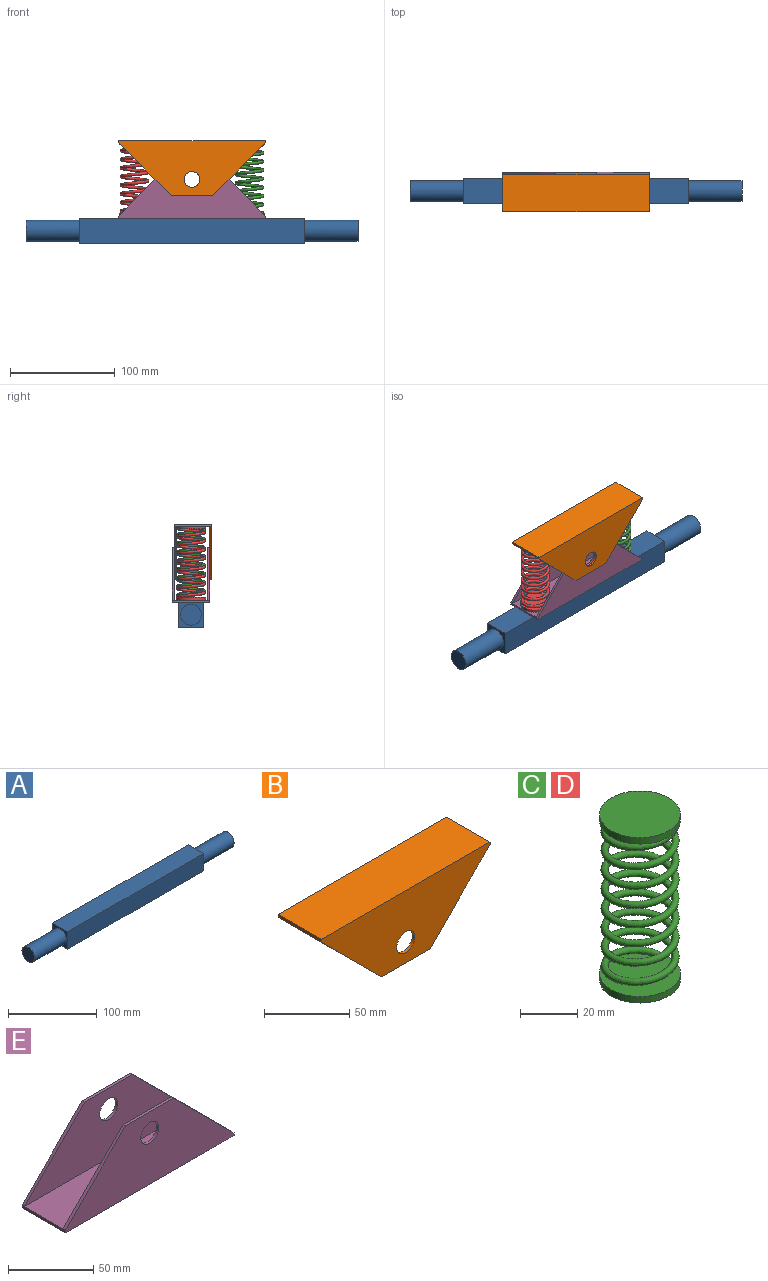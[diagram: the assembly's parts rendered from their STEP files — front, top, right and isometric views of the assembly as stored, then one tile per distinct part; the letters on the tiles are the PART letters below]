
ASSEMBLY  parts=5 mates=4
PART A: 10 faces, bbox 317.5x24x24 mm
  f0: plane 24x24mm, normal (1,0,0), area 261.8mm2, adj f2,f6,f7,f8,f9
  f1: plane 24x24mm, normal (-1,0,0), area 261.8mm2, adj f3,f6,f7,f8,f9
  f2: cylinder r=10mm len=50.8mm, axis (-1,0,0), area 3191.9mm2, adj f0,f4
  f3: cylinder r=10mm len=50.8mm, axis (-1,0,0), area 3191.9mm2, adj f1,f5
  f4: plane 20x20mm, normal (1,0,0), area 314.2mm2, adj f2
  f5: plane 20x20mm, normal (-1,0,0), area 314.2mm2, adj f3
  f6: plane 215.9x24mm, normal (0,0,1), area 5181.6mm2, adj f0,f1,f7,f8
  f7: plane 215.9x24mm, normal (0,-1,0), area 5181.6mm2, adj f0,f1,f6,f9
  f8: plane 215.9x24mm, normal (0,1,0), area 5181.6mm2, adj f0,f1,f6,f9
  f9: plane 215.9x24mm, normal (0,0,-1), area 5181.6mm2, adj f0,f1,f7,f8
PART B: 16 faces, bbox 140x36x52 mm
  f0: plane 50x50mm, normal (-0.71,0,-0.71), area 141.4mm2, adj f1,f4,f5,f13
  f1: plane 40x2mm, normal (0,0,-1), area 80mm2, adj f0,f3,f4,f5
  f2: cylinder r=7.5mm len=15mm, axis (0,1,0), area 94.2mm2, adj f4,f5
  f3: plane 50x50mm, normal (0.71,0,-0.71), area 141.4mm2, adj f1,f4,f5,f14
  f4: plane 140x52mm, normal (0,-1,0), area 4603.3mm2, adj f0,f1,f2,f3,f13,f14,f15
  f5: plane 140x50mm, normal (0,1,0), area 4323.3mm2, adj f0,f1,f2,f3,f12
  f6: plane 50x50mm, normal (-0.71,0,-0.71), area 141.4mm2, adj f7,f10,f11,f13
  f7: plane 40x2mm, normal (0,0,-1), area 80mm2, adj f6,f9,f10,f11
  f8: cylinder r=7.5mm len=15mm, axis (0,1,0), area 94.2mm2, adj f10,f11
  f9: plane 50x50mm, normal (0.71,0,-0.71), area 141.4mm2, adj f7,f10,f11,f14
  f10: plane 140x50mm, normal (0,-1,0), area 4323.3mm2, adj f6,f7,f8,f9,f12
  f11: plane 140x52mm, normal (0,1,0), area 4603.3mm2, adj f6,f7,f8,f9,f13,f14,f15
  f12: plane 140x32mm, normal (0,0,-1), area 4480mm2, adj f5,f10,f13,f14
  f13: plane 36x2mm, normal (-1,0,0), area 72mm2, adj f0,f4,f6,f11,f12,f15
  f14: plane 36x2mm, normal (1,0,0), area 72mm2, adj f3,f4,f9,f11,f12,f15
  f15: plane 140x36mm, normal (0,0,1), area 5040mm2, adj f4,f11,f13,f14
PART C: 9 faces, bbox 28.7x28.7x71.5 mm
  f0: plane 28.36x28.36mm, normal (0,0,-1), area 589mm2, adj f1,f3,f4
  f1: cylinder r=14.12mm len=28.25mm, axis (0,0,-1), area 242.7mm2, adj f0,f2
  f2: plane 28.25x28.25mm, normal (0,0,1), area 626.7mm2, adj f1
  f3: plane 2.27x0.71mm, normal (0,1,0), area 0.9mm2, adj f0,f4
  f4: bspline ~70.91x27.31mm, area 4878mm2, adj f0,f3,f5,f8
  f5: plane 2.89x1.62mm, normal (0,-1,0), area 2.5mm2, adj f4,f8
  f6: cylinder r=14.17mm len=28.34mm, axis (0,0,1), area 244.3mm2, adj f7,f8
  f7: plane 28.34x28.34mm, normal (0,0,-1), area 630.8mm2, adj f6
  f8: plane 28.34x28.34mm, normal (0,0,1), area 607mm2, adj f4,f5,f6
PART D: same geometry as C
PART E: 16 faces, bbox 140x36x52 mm
  f0: plane 140x32mm, normal (0,0,1), area 4480mm2, adj f5,f7,f8,f15
  f1: plane 50x50mm, normal (-0.71,0,0.71), area 141.4mm2, adj f2,f5,f6,f7
  f2: plane 40x2mm, normal (0,0,1), area 80mm2, adj f1,f4,f5,f6
  f3: cylinder r=7.5mm len=15mm, axis (0,-1,0), area 94.2mm2, adj f5,f6
  f4: plane 50x50mm, normal (0.71,0,0.71), area 141.4mm2, adj f2,f5,f6,f8
  f5: plane 140x50mm, normal (0,1,0), area 4323.3mm2, adj f0,f1,f2,f3,f4
  f6: plane 140x52mm, normal (0,-1,0), area 4603.3mm2, adj f1,f2,f3,f4,f7,f8,f9
  f7: plane 36x2mm, normal (-1,0,0), area 72mm2, adj f0,f1,f6,f9,f10,f11
  f8: plane 36x2mm, normal (1,0,0), area 72mm2, adj f0,f4,f6,f9,f10,f14
  f9: plane 140x36mm, normal (0,0,-1), area 5040mm2, adj f6,f7,f8,f10
  f10: plane 140x52mm, normal (0,1,0), area 4603.3mm2, adj f7,f8,f9,f11,f12,f13,f14
  f11: plane 50x50mm, normal (-0.71,0,0.71), area 141.4mm2, adj f7,f10,f12,f15
  f12: plane 40x2mm, normal (0,0,1), area 80mm2, adj f10,f11,f14,f15
  f13: cylinder r=7.5mm len=15mm, axis (0,-1,0), area 94.2mm2, adj f10,f15
  f14: plane 50x50mm, normal (0.71,0,0.71), area 141.4mm2, adj f8,f10,f12,f15
  f15: plane 140x50mm, normal (0,-1,0), area 4323.3mm2, adj f0,f11,f12,f13,f14
PLACE A t=(95.07,25,-18.55)mm
PLACE B t=(92.59,41,32.35)mm
PLACE C t=(150.07,25,-1.8)mm
PLACE D rot(axis=(0,0,1),90deg) t=(40.07,25,-1.8)mm
PLACE E t=(95.25,79,60.15)mm
MATE fastened E.f9 <-> A.f6  axis (0,0,-1) through (95.07,25,-6.55)mm
MATE fastened D.f1 <-> E.f0  axis (0,0,-1) through (40.07,25,-4.55)mm
MATE fastened C.f1 <-> E.f0  axis (0,0,-1) through (150.07,25,-4.55)mm
MATE revolute E.f13 <-> B.f2  axis (0,-1,0) through (95.07,41,30.45)mm
